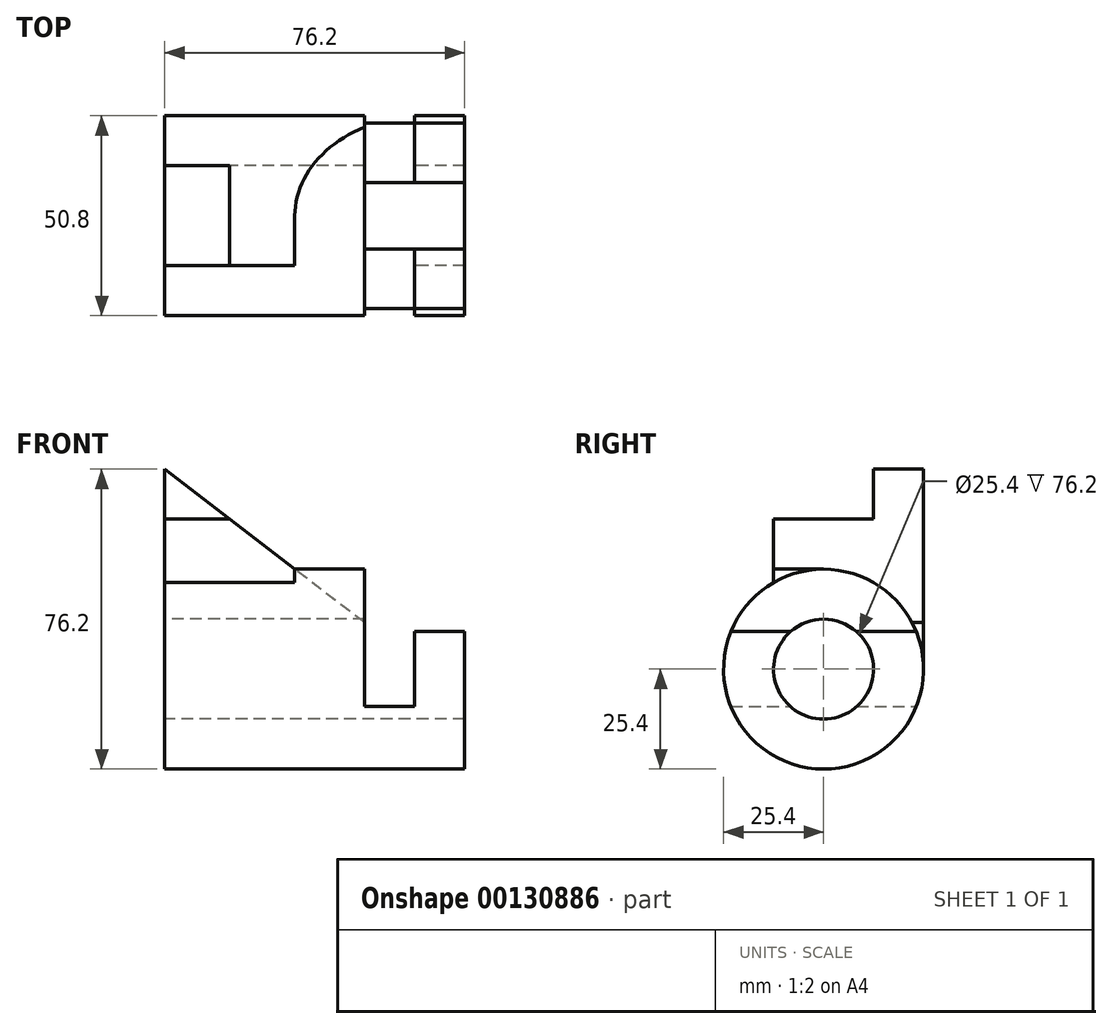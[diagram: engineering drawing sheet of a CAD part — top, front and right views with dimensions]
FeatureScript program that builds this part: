
annotation { "Feature Type Name" : "Feature", "Feature Type Description" : "" }
export const myFeature = defineFeature(function(context is Context, id is Id, definition is map)
    precondition{}
    {
        {
            var Q0;
            Q0=qCreatedBy(makeId("Right.planeOp"),FACE);
            var sketch = newSketch(context, id + "F0", { "sketchPlane" : qUnion([Q0])});
            skCircle(sketch, "E0", {"center": v(0, 0) * mm, "radius": 12.7 * mm});
            skCircle(sketch, "E1", {"center": v(0, 0) * mm, "radius": 25.4 * mm});
            skLineSegment(sketch, "E2", {"start": v(-12.7, 22) * mm, "end": v(-12.7, 38.1) * mm});
            skLineSegment(sketch, "E3", {"start": v(-12.7, 38.1) * mm, "end": v(12.7, 38.1) * mm});
            skLineSegment(sketch, "E4", {"start": v(12.7, 38.1) * mm, "end": v(12.7, 50.8) * mm});
            skLineSegment(sketch, "E5", {"start": v(12.7, 50.8) * mm, "end": v(25.4, 50.8) * mm});
            skLineSegment(sketch, "E6", {"start": v(25.4, 50.8) * mm, "end": v(25.4, 0) * mm});
            skLineSegment(sketch, "E7", {"start": v(-23.55, 9.53) * mm, "end": v(-8.4, 9.53) * mm});
            skLineSegment(sketch, "E8", {"start": v(-8.4, 9.53) * mm, "end": v(8.4, 9.53) * mm, "construction": true});
            skLineSegment(sketch, "E9", {"start": v(8.4, 9.53) * mm, "end": v(23.55, 9.53) * mm});
            skLineSegment(sketch, "E10", {"start": v(-23.55, -9.53) * mm, "end": v(-8.4, -9.53) * mm});
            skLineSegment(sketch, "E11", {"start": v(-8.4, -9.53) * mm, "end": v(8.4, -9.53) * mm, "construction": true});
            skLineSegment(sketch, "E12", {"start": v(8.4, -9.53) * mm, "end": v(23.55, -9.53) * mm});
            skArc(sketch, "E13", {"start": v(-8.4, -9.53) * mm, "mid": v(0, -12.7) * mm, "end": v(8.4, -9.53) * mm});
            skArc(sketch, "E14", {"start": v(-23.55, -9.53) * mm, "mid": v(0, -25.4) * mm, "end": v(23.55, -9.53) * mm});
            skSolve(sketch);
        }
        {
            var Q0;
            {var subQ0=sQuery(id+"F0.wireOp",EDGE,"E7");Q0=makeQuery(id+"F0.imprint","IMPRINT",FACE,{"disambiguationData":[TD([[makeQuery(id+"F0.imprint","IMPRINT",EDGE,{"derivedFrom":subQ0}),1.0]])]});}
            var Q1;
            {var subQ0=sQuery(id+"F0.wireOp",EDGE,"E7");Q1=makeQuery(id+"F0.imprint","IMPRINT",FACE,{"disambiguationData":[TD([[makeQuery(id+"F0.imprint","IMPRINT",EDGE,{"derivedFrom":subQ0}),-1.0]])]});}
            extrude(context, id + "F1", {"entities" : qUnion([Q0, Q1]), "depth" : 50.8 * mm});
        }
        {
            var Q0;
            {var subQ1=sQuery(id+"F0.wireOp",EDGE,"E10");Q0=makeQuery(id+"F0.imprint","IMPRINT",FACE,{"disambiguationData":[TD([[makeQuery(id+"F0.imprint","IMPRINT",EDGE,{"derivedFrom":subQ1}),-1.0]])]});}
            extrude(context, id + "F2", {"entities" : qUnion([Q0]), "operationType" : NewBodyOperationType.ADD, "depth" : 63.5 * mm});
        }
        {
            var Q0;
            {var subQ0=sQuery(id+"F0.wireOp",EDGE,"E2");Q0=makeQuery(id+"F0.imprint","IMPRINT",FACE,{"disambiguationData":[TD([[makeQuery(id+"F0.imprint","IMPRINT",EDGE,{"derivedFrom":subQ0}),-1.0]])]});}
            extrude(context, id + "F3", {"entities" : qUnion([Q0]), "operationType" : NewBodyOperationType.ADD, "depth" : 33.02 * mm});
        }
        {
            var Q0;
            Q0=makeQuery(id+"F3.opExtrude","SWEPT_FACE",FACE,{"disambiguationData":[OSD([sQuery(id+"F0.wireOp",EDGE,"E6")])]});
            var sketch = newSketch(context, id + "F4", { "sketchPlane" : qUnion([Q0])});
            skLineSegment(sketch, "E15", {"start": v(-33.02, 25.4) * mm, "end": v(0, 50.8) * mm});
            skLineSegment(sketch, "E16", {"start": v(0, 50.8) * mm, "end": v(-33.02, 50.8) * mm});
            skLineSegment(sketch, "E17", {"start": v(-33.02, 50.8) * mm, "end": v(-33.02, 25.4) * mm});
            skSolve(sketch);
        }
        {
            var Q0;
            Q0=makeQuery(id+"F4.imprint","IMPRINT",FACE,{"disambiguationData":[TD([[makeQuery(id+"F4.imprint","IMPRINT",EDGE,{"derivedFrom":sQuery(id+"F4.wireOp",EDGE,"E15")}),1.0]])]});
            extrude(context, id + "F5", {"entities" : qUnion([Q0]), "operationType" : NewBodyOperationType.REMOVE, "endBound" : BoundingType.THROUGH_ALL, "oppositeDirection" : true, "depth" : 25.4 * mm});
        }
        {
            var Q0;
            {var subQ1=sQuery(id+"F0.wireOp",EDGE,"E10");Q0=makeQuery(id+"F0.imprint","IMPRINT",FACE,{"disambiguationData":[TD([[makeQuery(id+"F0.imprint","IMPRINT",EDGE,{"derivedFrom":subQ1}),-1.0]])]});}
            var Q1;
            {var subQ0=sQuery(id+"F0.wireOp",EDGE,"E7");Q1=makeQuery(id+"F0.imprint","IMPRINT",FACE,{"disambiguationData":[TD([[makeQuery(id+"F0.imprint","IMPRINT",EDGE,{"derivedFrom":subQ0}),-1.0]])]});}
            var Q2;
            {var subQ3=sQuery(id+"F0.wireOp",EDGE,"E9");Q2=makeQuery(id+"F0.imprint","IMPRINT",FACE,{"disambiguationData":[TD([[makeQuery(id+"F0.imprint","IMPRINT",EDGE,{"derivedFrom":subQ3}),-1.0]])]});}
            extrude(context, id + "F6", {"entities" : qUnion([Q0, Q1, Q2]), "operationType" : NewBodyOperationType.ADD, "depth" : 50.8 * mm});
        }
        {
            var Q0;
            Q0=makeQuery(id+"F2.opExtrude","CAP_FACE",FACE,{"disambiguationData":[OSD([sQuery(id+"F0.wireOp",EDGE,"E0"),sQuery(id+"F0.wireOp",EDGE,"E1"),sQuery(id+"F0.wireOp",EDGE,"E10"),sQuery(id+"F0.wireOp",EDGE,"E12")])],"isStart":false});
            var sketch = newSketch(context, id + "F7", { "sketchPlane" : qUnion([Q0])});
            skCircle(sketch, "E18", {"center": v(0, 0) * mm, "radius": 25.4 * mm});
            skCircle(sketch, "E19", {"center": v(0, 0) * mm, "radius": 12.7 * mm});
            skLineSegment(sketch, "E20", {"start": v(-23.55, 9.53) * mm, "end": v(-8.4, 9.53) * mm});
            skLineSegment(sketch, "E21", {"start": v(-8.4, 9.53) * mm, "end": v(8.4, 9.53) * mm, "construction": true});
            skLineSegment(sketch, "E22", {"start": v(8.4, 9.53) * mm, "end": v(23.55, 9.53) * mm});
            skSolve(sketch);
        }
        {
            var Q0;
            {var subQ2=sQuery(id+"F7.wireOp",EDGE,"E20");Q0=makeQuery(id+"F7.imprint","IMPRINT",FACE,{"disambiguationData":[TD([[makeQuery(id+"F7.imprint","IMPRINT",EDGE,{"derivedFrom":subQ2}),-1.0]])]});}
            var Q1;
            {var subQ1=makeQuery(id+"F2.opExtrude","CAP_EDGE",EDGE,{"disambiguationData":[OSD([sQuery(id+"F0.wireOp",EDGE,"E10")])],"isStart":false});Q1=makeQuery(id+"F7.imprint","IMPRINT",FACE,{"disambiguationData":[TD([[makeQuery(id+"F7.imprint","IMPRINT",EDGE,{"derivedFrom":subQ1}),-1.0]])]});}
            var Q2;
            {var subQ2=sQuery(id+"F7.wireOp",EDGE,"E22");Q2=makeQuery(id+"F7.imprint","IMPRINT",FACE,{"disambiguationData":[TD([[makeQuery(id+"F7.imprint","IMPRINT",EDGE,{"derivedFrom":subQ2}),-1.0]])]});}
            extrude(context, id + "F8", {"entities" : qUnion([Q0, Q1, Q2]), "operationType" : NewBodyOperationType.ADD, "depth" : 12.7 * mm});
        }
        {
            var Q0;
            Q0=makeQuery(id+"F3.opExtrude","SWEPT_FACE",FACE,{"disambiguationData":[OSD([sQuery(id+"F0.wireOp",EDGE,"E6")])]});
            var sketch = newSketch(context, id + "F9", { "sketchPlane" : qUnion([Q0])});
            skLineSegment(sketch, "E23", {"start": v(0, 50.8) * mm, "end": v(-33.02, 25.4) * mm});
            skLineSegment(sketch, "E24", {"start": v(-33.02, 25.4) * mm, "end": v(-66.04, 0) * mm});
            skLineSegment(sketch, "E25", {"start": v(-66.04, 0) * mm, "end": v(0, 0) * mm});
            skLineSegment(sketch, "E26", {"start": v(-50.69, 0) * mm, "end": v(-50.69, 11.81) * mm});
            skLineSegment(sketch, "E27", {"start": v(-50.69, 11.81) * mm, "end": v(-33.02, 25.4) * mm});
            skLineSegment(sketch, "E28", {"start": v(0, 50.8) * mm, "end": v(0, 0) * mm});
            skSolve(sketch);
        }
        {
            var Q0;
            {var subQ2=sQuery(id+"F9.wireOp",EDGE,"E26");Q0=makeQuery(id+"F9.imprint","IMPRINT",FACE,{"disambiguationData":[TD([[makeQuery(id+"F9.imprint","IMPRINT",EDGE,{"derivedFrom":subQ2}),-1.0]])]});}
            extrude(context, id + "F10", {"entities" : qUnion([Q0]), "operationType" : NewBodyOperationType.ADD, "endBound" : BoundingType.UP_TO_NEXT, "oppositeDirection" : true, "depth" : 25.4 * mm});
        }
    });
